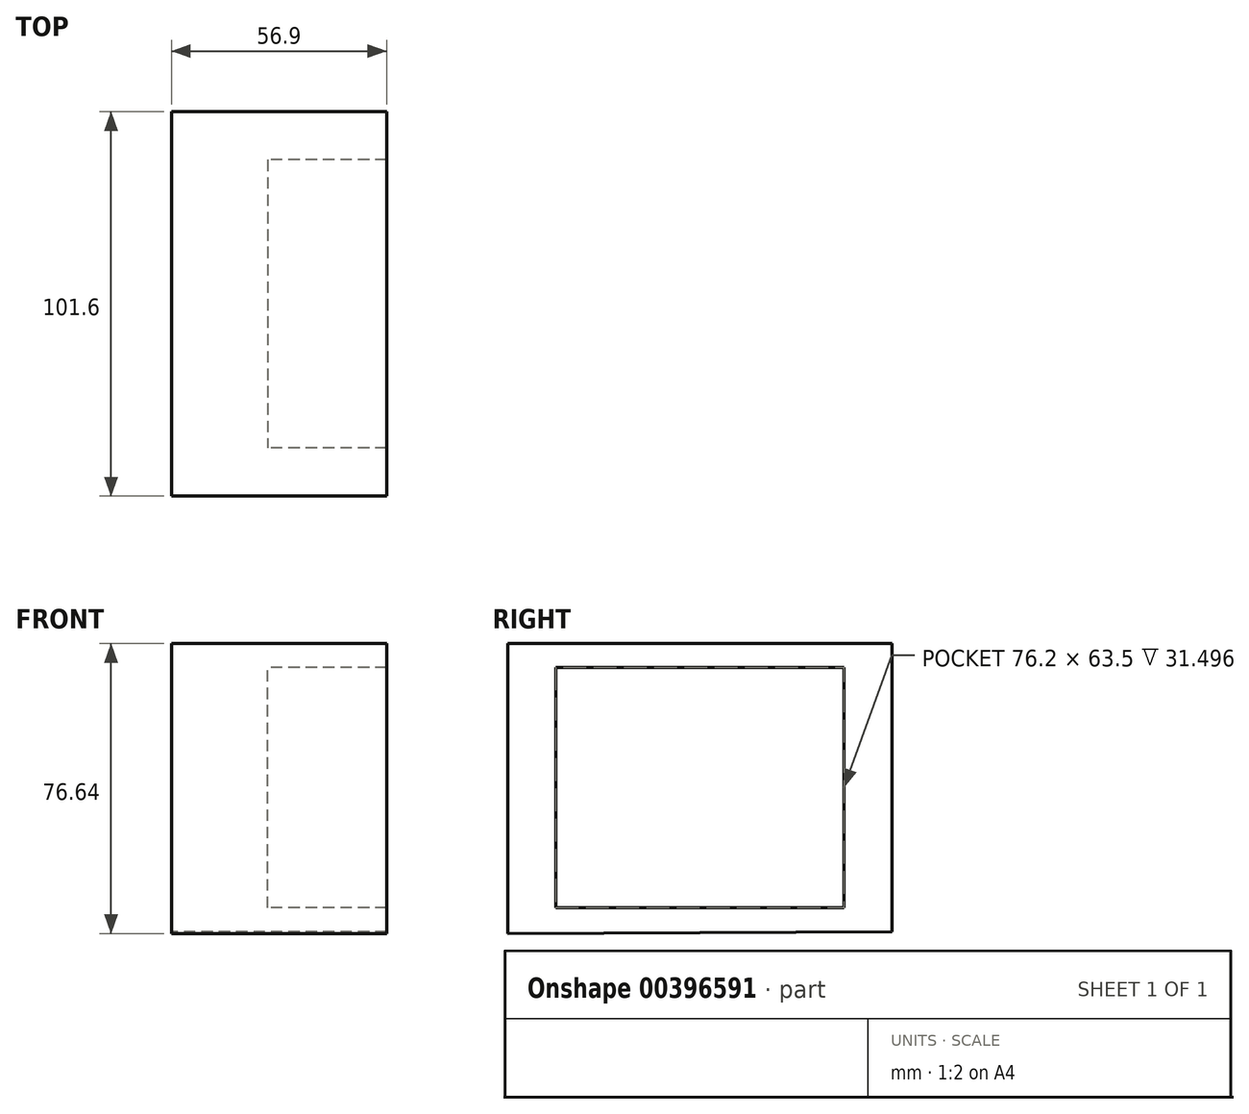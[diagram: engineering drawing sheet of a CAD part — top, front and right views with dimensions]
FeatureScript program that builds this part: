
annotation { "Feature Type Name" : "Feature", "Feature Type Description" : "" }
export const myFeature = defineFeature(function(context is Context, id is Id, definition is map)
    precondition{}
    {
        {
            var Q0;
            Q0=qCreatedBy(makeId("Right.planeOp"),FACE);
            var sketch = newSketch(context, id + "F0", { "sketchPlane" : qUnion([Q0])});
            skLineSegment(sketch, "E0", {"start": v(-48.98, -43.27) * mm, "end": v(-48.98, 20.23) * mm});
            skLineSegment(sketch, "E1", {"start": v(-48.98, 20.23) * mm, "end": v(27.22, 20.23) * mm});
            skLineSegment(sketch, "E2", {"start": v(27.22, 20.23) * mm, "end": v(27.22, -43.27) * mm});
            skLineSegment(sketch, "E3", {"start": v(27.22, -43.27) * mm, "end": v(-48.98, -43.27) * mm});
            skLineSegment(sketch, "E4", {"start": v(39.92, -49.62) * mm, "end": v(39.92, 26.58) * mm});
            skLineSegment(sketch, "E5", {"start": v(39.92, 26.58) * mm, "end": v(-61.68, 26.58) * mm});
            skLineSegment(sketch, "E6", {"start": v(-61.68, 26.58) * mm, "end": v(-61.68, -50.06) * mm});
            skLineSegment(sketch, "E7", {"start": v(-61.68, -50.06) * mm, "end": v(39.92, -49.62) * mm});
            skSolve(sketch);
        }
        {
            var Q0;
            Q0=makeQuery(id+"F0.imprint","IMPRINT",FACE,{"disambiguationData":[TD([[makeQuery(id+"F0.imprint","IMPRINT",EDGE,{"derivedFrom":sQuery(id+"F0.wireOp",EDGE,"E0")}),1.0]])]});
            extrude(context, id + "F1", {"entities" : qUnion([Q0]), "depth" : 56.9 * mm});
        }
        {
            var Q0;
            Q0=makeQuery(id+"F0.imprint","IMPRINT",FACE,{"disambiguationData":[TD([[makeQuery(id+"F0.imprint","IMPRINT",EDGE,{"derivedFrom":sQuery(id+"F0.wireOp",EDGE,"E0")}),-1.0]])]});
            extrude(context, id + "F2", {"entities" : qUnion([Q0]), "operationType" : NewBodyOperationType.ADD, "depth" : 25.4 * mm});
        }
    });
